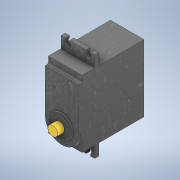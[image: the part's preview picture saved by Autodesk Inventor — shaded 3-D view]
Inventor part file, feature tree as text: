
AUTODESK INVENTOR PART (.ipt)
format: ipt  version: 2021 (Build 250183000, 183)  size: 224,768 bytes
history: native  units: mm
features: extrude x7, sketch x7, fillet x2, plane x1
ambient origin geometry x8: Origin, YZ Plane, XZ Plane, XY Plane, X Axis, Y Axis, Z Axis, Center Point
bodies: Solid1 (feature_tree)
feature tree (17):
  extrude  "Extrusion1"  Depth=40.0mm
  plane  "Work Plane1"
  extrude  "Extrusion2"  [1 undecoded]
  extrude  "Extrusion3"  Depth=3.9mm
  fillet  "Fillet1"  Radius=3.9mm
  fillet  "Fillet2"  Radius=3.8mm
  extrude  "Extrusion4"  Depth=2.5mm
  extrude  "Extrusion5"  Depth=2.0mm TaperAngle=0.0deg
  extrude  "Extrusion6"  Depth=1.0mm
  extrude  "Extrusion7"  Depth=1.0mm TaperAngle=0.0deg
  sketch  "Sketch1"  dims[d0=20.0mm d1=40.0mm]
  sketch  "Sketch2"  dims[d2=36.0mm d3=0.0mm d4=-10.0mm]
  sketch  "Sketch5"  dims[d5=6.8mm d6=3.9mm d7=3.9mm d8=3.8mm]
  sketch  "Sketch6"  dims[d9=3.8mm d10=2.5mm d11=2.5mm]
  sketch  "Sketch7"  dims[d12=2.5mm d13=0.0mm d14=2.0mm d15=0.0mm]
  sketch  "Sketch8"  dims[d16=1.0mm d17=1.0mm]
  sketch  "Sketch9"  dims[d18=13.5mm d19=1.0mm d20=0.0mm d21=11.0mm d22=0.5mm d23=0.0mm d24=5.8mm d25=4.0mm d26=0.0mm d27=1.0mm d28=0.0mm]
note: 1 required parameter value undecoded (feature->parameter linkage not recoverable at this tier; creation-order binding heuristic only, values carry confidence <= 0.55)
